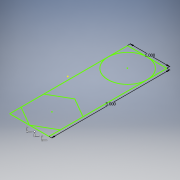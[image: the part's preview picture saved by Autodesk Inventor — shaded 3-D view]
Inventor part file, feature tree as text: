
AUTODESK INVENTOR PART (.ipt)
format: ipt  version: 2018 (Build 220112000, 112)  size: 93,696 bytes
history: native  units: in
note: dims shown in document units (in); Inventor stores cm internally (conversion verified against a paired STEP export)
features: sketch x1
ambient origin geometry x8: Origin, YZ Plane, XZ Plane, XY Plane, X Axis, Y Axis, Z Axis, Center Point
feature tree (1):
  sketch  "Sketch2"  dims[d2=1.0in d3=3.0in]
